# Revit family: Projector-Canon-REALiS_WUX6010(D)_Pro_AV-WUX6500(D)_Pro_AV-02
name_source: partatom
category: Communication Devices
revit_build: Autodesk Revit 2015 (Build: 20140903_1530(x64)
units: mm (PartAtom-declared; Revit-internal decimal feet)

## types (1)
- Not A Type - Load Type Catalog
    Analog PC Input = WUXGA / UXGA / WSXGA+ / SXGA+ / WXGA+ / FWXGA / WXGA / SXGA / XGA / SVGA / VGA
    Apparent Load = 0 VA
    Assembly Code = D5030900
    Brightness = 6009 Lumens (Normal) / 4660 Lumens (Power Saver)
    C Lens = 1
    C Lens Shift = No
    C Projector H = 73' - 3 9/32"
    Component Video Input = 1080p / 1080i / 720p / 576p / 576i / 480p / 480i
    Contrast = 2000:1
    Default Elevation = 4' - 0"
    Depth = 1' - 4 15/16"
    Description = The new REALiS WUX6010 projector offers a robust combination of 6000 Lumens of high brightness, WUXGA (1920 x 1200) high resolution, and Canon's unique LCOS display technology to set this model apart. The REALiS WUX6010 Pro AV Installation LCOS Projector delivers intricately detailed, color-accurate still or motion images with a contrast ratio of up to 2000:1.This model is compatible with all current interchangeable Genuine Canon projector lenses to suit a variety of screen sizes.
    Digital PC Input = WUXGA / UXGA / WSXGA+ / SXGA+ / WXGA+ / FWXGA / WXGA / SXGA / XGA / SVGA / VGA
    Digital Video Input = 1080p / 1080i / 720p / 576p / 480p
    F-Number = 1.99 - 2.83
    Fan Noise = 40dB (Full Power) / 36dB (Power Saver)
    Focal Length = 34.0 - 57.7 mm, 1.7x Optical Zoom
    Height = 0' - 6 11/16"
    Keynote = Division 27
    Lens Shift = Motorized
    Lens Shift (Horizontal) = Left 10% to Right 10%
    Lens Shift (Vertical) = Down 15% to Up 55%
    Manufacturer = Canon USA Inc.
    Model = WUX6010
    Model Disclaimer = This 3D model is a simulation of a highly customizable piece of Canon equipment. For assistance in selecting the right Canon equipment for your project, please contact Canon U.S.A., Inc.
    Mounting = 360° projection
    Native Resolution = 1920 x 1200 (WUXGA)
    Number of Poles = 1
    Operating Temperature = 32°F - 104°F (0°C - 40°C) (20%RH - 85%RH)
    Power Consumption = 465W/370 W
    Power Factor = 1
    Power Voltage = AC 100 ~ 240V, 50/60 Hz
    Product Documentation Link = https://www.usa.canon.com
    Product Name = REALiS WUX6010 Pro AV
    Product Page URL = https://www.usa.canon.com
    Projection Distances = 6.23 - 159.12 ft. (1.9 - 48.5 m)
    Scanning Frequency = H: 27 ~ 75 kHz, V: 24 ~ 60Hz
    Screen Sizes = 40" - 600"
    Standby Power = 2.0 ~ 0.3W
    Throw Ratio = 2.19 - 3.74:1
    Tilt Angle = Bottom Front Feet: 2 places (Max. angles: 6° elevation)
    Type Comments = -
    URL = http://projectors.usa.canon.com
    Version = 2015 – v1.0a
    Voltage = 100 V
    Weight = 18.73 lb
    Width = 1' - 2 31/32"

## geometry (parser evidence)
native form markers: Sweep x6
no freeform markers — native parametric forms only
